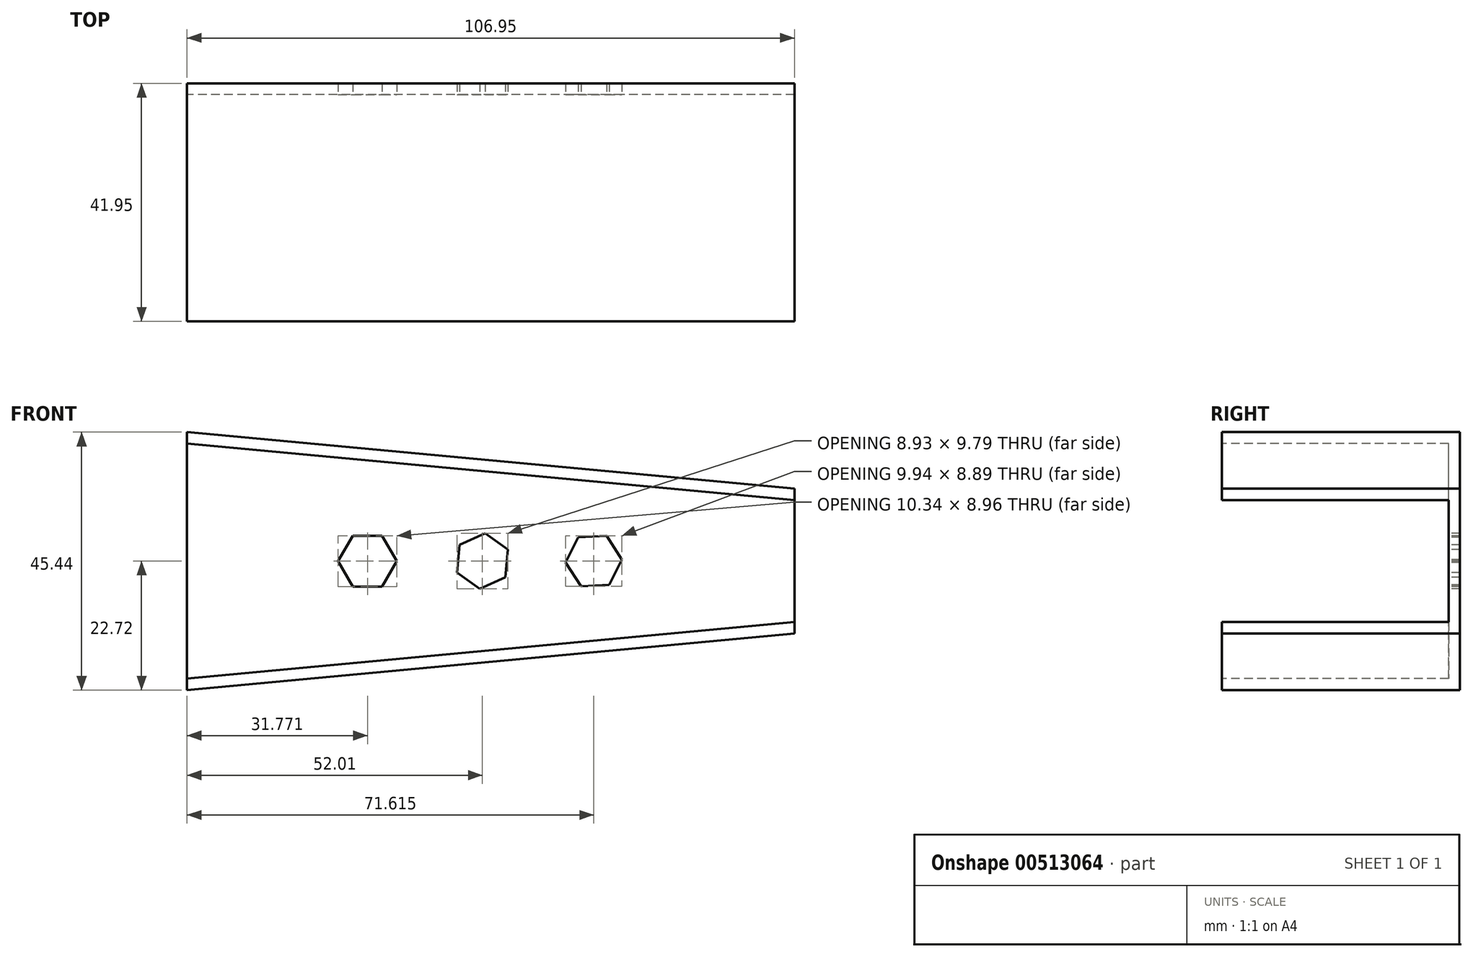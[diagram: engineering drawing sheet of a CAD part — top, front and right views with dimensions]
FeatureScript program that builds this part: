
annotation { "Feature Type Name" : "Feature", "Feature Type Description" : "" }
export const myFeature = defineFeature(function(context is Context, id is Id, definition is map)
    precondition{}
    {
        {
            var Q0;
            Q0=qCreatedBy(makeId("Front.planeOp"),FACE);
            var sketch = newSketch(context, id + "F0", { "sketchPlane" : qUnion([Q0])});
            skLineSegment(sketch, "E0", {"start": v(54.94, 0) * mm, "end": v(54.94, 12.76) * mm});
            skLineSegment(sketch, "E1", {"start": v(54.94, 0) * mm, "end": v(54.94, -12.74) * mm});
            skLineSegment(sketch, "E2", {"start": v(-52.01, -22.72) * mm, "end": v(-52.01, 22.72) * mm});
            skLineSegment(sketch, "E3", {"start": v(-52.01, 22.72) * mm, "end": v(54.94, 12.76) * mm});
            skLineSegment(sketch, "E4", {"start": v(-52.01, -22.72) * mm, "end": v(54.94, -12.74) * mm});
            skSolve(sketch);
        }
        {
            var Q0;
            Q0=makeQuery(id+"F0.imprint","IMPRINT",FACE,{"disambiguationData":[TD([[makeQuery(id+"F0.imprint","IMPRINT",EDGE,{"derivedFrom":sQuery(id+"F0.wireOp",EDGE,"E0")}),1.0]])]});
            extrude(context, id + "F1", {"entities" : qUnion([Q0]), "depth" : 41.95 * mm, "offsetDistance" : 25 * mm});
        }
        {
            var Q0;
            Q0=makeQuery(id+"F1.opExtrude","CAP_FACE",FACE,{"disambiguationData":[OSD([sQuery(id+"F0.wireOp",EDGE,"E0"),sQuery(id+"F0.wireOp",EDGE,"E1"),sQuery(id+"F0.wireOp",EDGE,"E2"),sQuery(id+"F0.wireOp",EDGE,"E3"),sQuery(id+"F0.wireOp",EDGE,"E4")])],"isStart":false});
            var sketch = newSketch(context, id + "F2", { "sketchPlane" : qUnion([Q0])});
            skLineSegment(sketch, "E5", {"start": v(-52.01, 22.72) * mm, "end": v(-52.01, 20.72) * mm});
            skLineSegment(sketch, "E6", {"start": v(-52.01, 20.72) * mm, "end": v(-52.01, -20.72) * mm});
            skLineSegment(sketch, "E7", {"start": v(54.94, -10.74) * mm, "end": v(-52.01, -20.72) * mm});
            skLineSegment(sketch, "E8", {"start": v(54.94, 10.76) * mm, "end": v(-52.01, 20.72) * mm});
            skLineSegment(sketch, "E9", {"start": v(54.94, 10.76) * mm, "end": v(54.94, -10.74) * mm});
            skSolve(sketch);
        }
        {
            var Q0;
            Q0=makeQuery(id+"F2.imprint","IMPRINT",FACE,{"disambiguationData":[TD([[makeQuery(id+"F2.imprint","IMPRINT",EDGE,{"derivedFrom":sQuery(id+"F2.wireOp",EDGE,"E6")}),-1.0]])]});
            extrude(context, id + "F3", {"entities" : qUnion([Q0]), "operationType" : NewBodyOperationType.REMOVE, "oppositeDirection" : true, "depth" : 39.95 * mm, "offsetDistance" : 25 * mm});
        }
        {
            var Q0;
            Q0=makeQuery(id+"F3.boolean.opBoolean","COPY",FACE,{"derivedFrom":makeQuery(id+"F3.opExtrude","CAP_FACE",FACE,{"disambiguationData":[OSD([sQuery(id+"F2.wireOp",EDGE,"E6"),sQuery(id+"F2.wireOp",EDGE,"E7"),sQuery(id+"F2.wireOp",EDGE,"E8"),sQuery(id+"F2.wireOp",EDGE,"E9")])],"isStart":false})});
            var sketch = newSketch(context, id + "F4", { "sketchPlane" : qUnion([Q0])});
            skCircle(sketch, "E10.cCircle", {"center": v(0, 0) * mm, "radius": 4.26 * mm, "construction": true});
            skLineSegment(sketch, "E10.0", {"start": v(4.47, 2.05) * mm, "end": v(4, -2.84) * mm});
            skLineSegment(sketch, "E10.1", {"start": v(4, -2.84) * mm, "end": v(-0.46, -4.9) * mm});
            skLineSegment(sketch, "E10.2", {"start": v(-0.46, -4.9) * mm, "end": v(-4.47, -2.05) * mm});
            skLineSegment(sketch, "E10.3", {"start": v(-4.47, -2.05) * mm, "end": v(-4, 2.84) * mm});
            skLineSegment(sketch, "E10.4", {"start": v(-4, 2.84) * mm, "end": v(0.46, 4.9) * mm});
            skLineSegment(sketch, "E10.5", {"start": v(0.46, 4.9) * mm, "end": v(4.47, 2.05) * mm});
            skPoint(sketch, "E10.0.midPoint", {"position": v(4.24, -0.4) * mm});
            skCircle(sketch, "E11.cCircle", {"center": v(-20.24, 0) * mm, "radius": 4.48 * mm, "construction": true});
            skLineSegment(sketch, "E11.0", {"start": v(-22.82, 4.48) * mm, "end": v(-17.65, 4.48) * mm});
            skLineSegment(sketch, "E11.1", {"start": v(-17.65, 4.48) * mm, "end": v(-15.07, 0) * mm});
            skLineSegment(sketch, "E11.2", {"start": v(-15.07, 0) * mm, "end": v(-17.65, -4.48) * mm});
            skLineSegment(sketch, "E11.3", {"start": v(-17.65, -4.48) * mm, "end": v(-22.82, -4.48) * mm});
            skLineSegment(sketch, "E11.4", {"start": v(-22.82, -4.48) * mm, "end": v(-25.4, 0) * mm});
            skLineSegment(sketch, "E11.5", {"start": v(-25.4, 0) * mm, "end": v(-22.82, 4.48) * mm});
            skPoint(sketch, "E11.0.midPoint", {"position": v(-20.24, 4.48) * mm});
            skCircle(sketch, "E12.cCircle", {"center": v(19.6, 0) * mm, "radius": 4.31 * mm, "construction": true});
            skLineSegment(sketch, "E12.0", {"start": v(21.85, 4.44) * mm, "end": v(24.58, 0.28) * mm});
            skLineSegment(sketch, "E12.1", {"start": v(24.58, 0.28) * mm, "end": v(22.33, -4.17) * mm});
            skLineSegment(sketch, "E12.2", {"start": v(22.33, -4.17) * mm, "end": v(17.36, -4.44) * mm});
            skLineSegment(sketch, "E12.3", {"start": v(17.36, -4.44) * mm, "end": v(14.63, -0.28) * mm});
            skLineSegment(sketch, "E12.4", {"start": v(14.63, -0.28) * mm, "end": v(16.88, 4.17) * mm});
            skLineSegment(sketch, "E12.5", {"start": v(16.88, 4.17) * mm, "end": v(21.85, 4.44) * mm});
            skPoint(sketch, "E12.0.midPoint", {"position": v(23.21, 2.36) * mm});
            skSolve(sketch);
        }
        {
            var Q0;
            Q0=makeQuery(id+"F4.imprint","IMPRINT",FACE,{"disambiguationData":[TD([[makeQuery(id+"F4.imprint","IMPRINT",EDGE,{"derivedFrom":sQuery(id+"F4.wireOp",EDGE,"E11.0")}),-1.0]])]});
            var Q1;
            Q1=makeQuery(id+"F4.imprint","IMPRINT",FACE,{"disambiguationData":[TD([[makeQuery(id+"F4.imprint","IMPRINT",EDGE,{"derivedFrom":sQuery(id+"F4.wireOp",EDGE,"E10.0")}),-1.0]])]});
            var Q2;
            Q2=makeQuery(id+"F4.imprint","IMPRINT",FACE,{"disambiguationData":[TD([[makeQuery(id+"F4.imprint","IMPRINT",EDGE,{"derivedFrom":sQuery(id+"F4.wireOp",EDGE,"E12.0")}),-1.0]])]});
            extrude(context, id + "F5", {"entities" : qUnion([Q0, Q1, Q2]), "operationType" : NewBodyOperationType.REMOVE, "oppositeDirection" : true, "depth" : 5 * mm, "offsetDistance" : 25 * mm});
        }
    });
